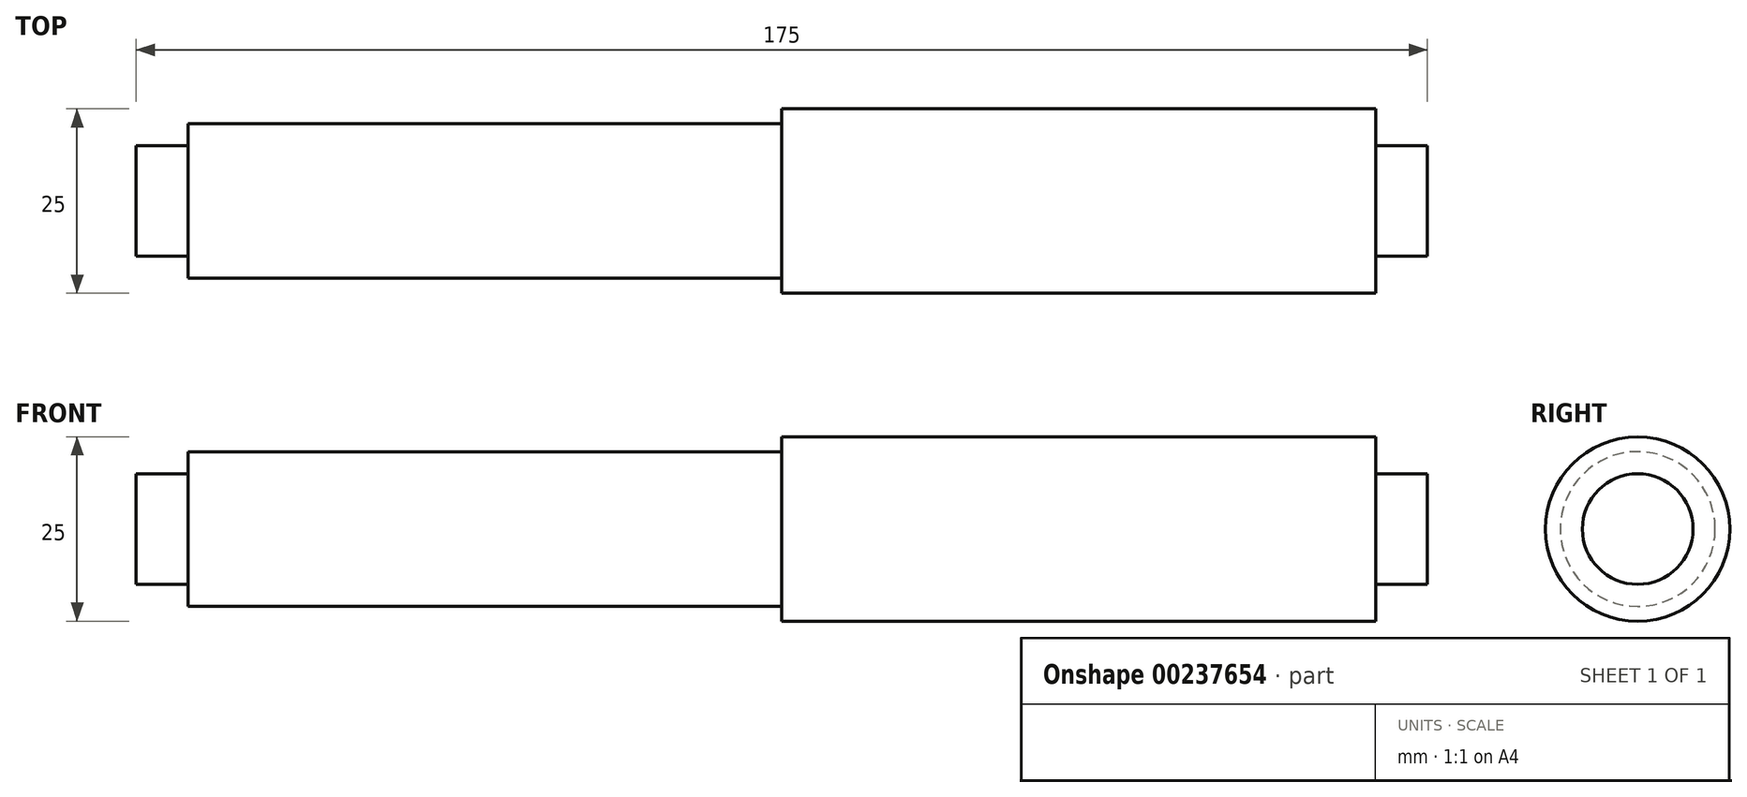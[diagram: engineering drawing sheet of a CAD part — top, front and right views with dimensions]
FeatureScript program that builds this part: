
annotation { "Feature Type Name" : "Feature", "Feature Type Description" : "" }
export const myFeature = defineFeature(function(context is Context, id is Id, definition is map)
    precondition{}
    {
        {
            var Q0;
            Q0=qCreatedBy(makeId("Front.planeOp"),FACE);
            var sketch = newSketch(context, id + "F0", { "sketchPlane" : qUnion([Q0])});
            skLineSegment(sketch, "E0", {"start": v(-87.5, 0) * mm, "end": v(-87.5, 7.5) * mm});
            skLineSegment(sketch, "E1", {"start": v(-87.5, 7.5) * mm, "end": v(-80.5, 7.5) * mm});
            skLineSegment(sketch, "E2", {"start": v(-80.5, 7.5) * mm, "end": v(-80.5, 10.5) * mm});
            skLineSegment(sketch, "E3", {"start": v(-80.5, 10.5) * mm, "end": v(0, 10.5) * mm});
            skLineSegment(sketch, "E4", {"start": v(0, 10.5) * mm, "end": v(0, 12.5) * mm});
            skLineSegment(sketch, "E5", {"start": v(0, 12.5) * mm, "end": v(80.5, 12.5) * mm});
            skLineSegment(sketch, "E6", {"start": v(80.5, 12.5) * mm, "end": v(80.5, 7.5) * mm});
            skLineSegment(sketch, "E7", {"start": v(80.5, 7.5) * mm, "end": v(87.5, 7.5) * mm});
            skLineSegment(sketch, "E8", {"start": v(87.5, 7.5) * mm, "end": v(87.5, 0) * mm});
            skLineSegment(sketch, "E9", {"start": v(87.5, 0) * mm, "end": v(-87.5, 0) * mm});
            skSolve(sketch);
        }
        {
            var Q0;
            Q0=makeQuery(id+"F0.imprint","IMPRINT",FACE,{"disambiguationData":[TD([[makeQuery(id+"F0.imprint","IMPRINT",EDGE,{"derivedFrom":sQuery(id+"F0.wireOp",EDGE,"E0")}),-1.0]])]});
            var Q1;
            Q1=sQuery(id+"F0.wireOp",EDGE,"E9");
            revolve(context, id + "F1", {"entities" : qUnion([Q0]), "axis" : qUnion([Q1]), "revolveType" : RevolveType.FULL});
        }
    });
